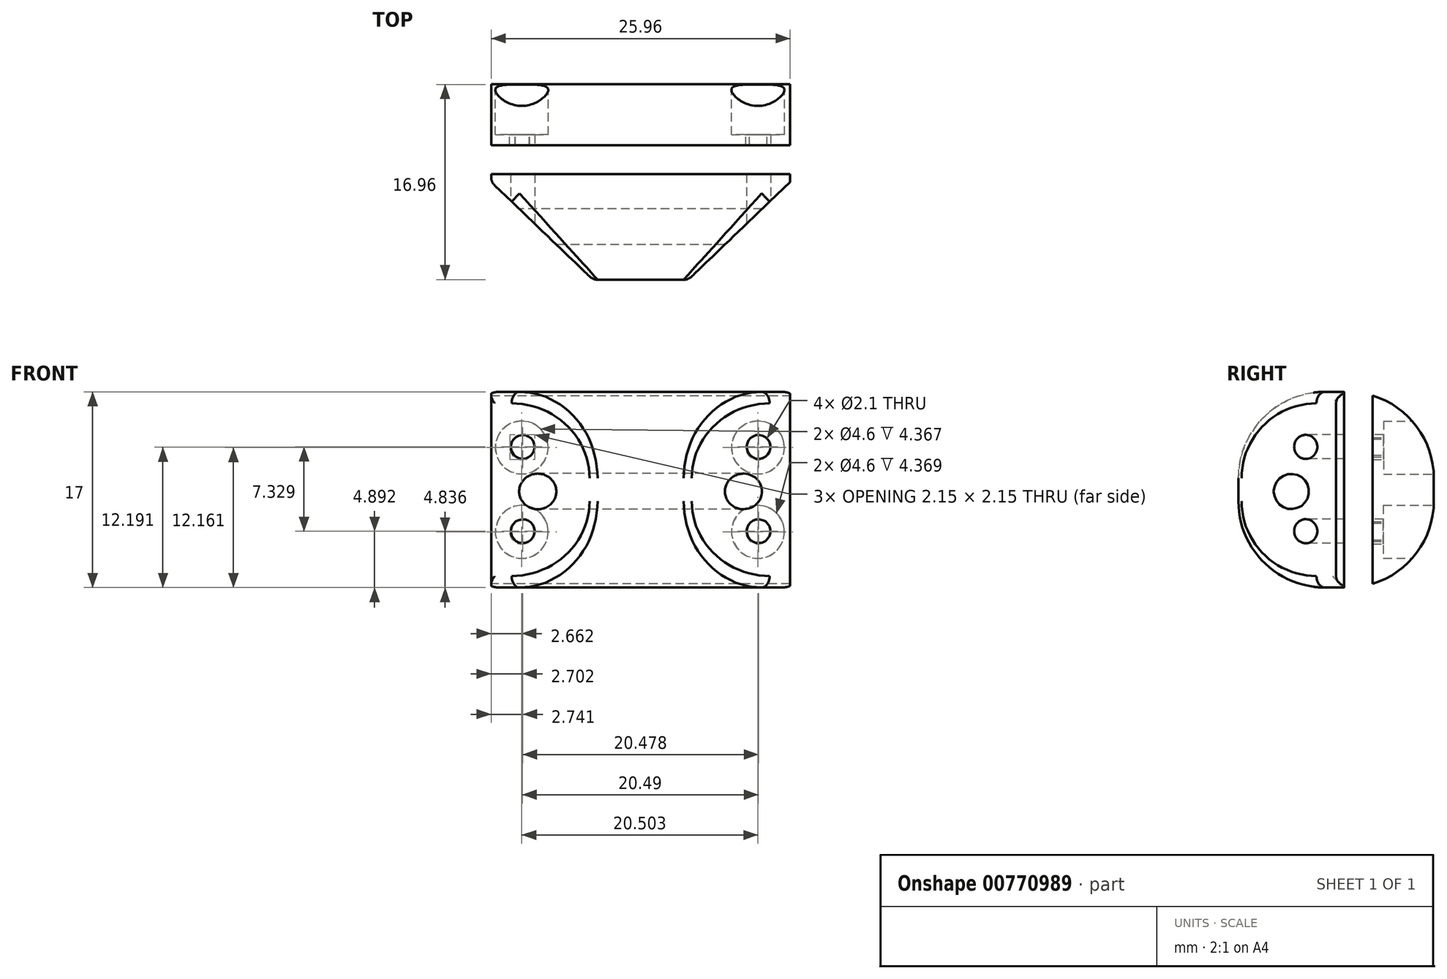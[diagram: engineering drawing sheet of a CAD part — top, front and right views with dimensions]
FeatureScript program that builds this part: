
annotation { "Feature Type Name" : "Feature", "Feature Type Description" : "" }
export const myFeature = defineFeature(function(context is Context, id is Id, definition is map)
    precondition{}
    {
        {
            var Q0;
            Q0=qCreatedBy(makeId("Top.planeOp"),FACE);
            var sketch = newSketch(context, id + "F0", { "sketchPlane" : qUnion([Q0])});
            skLineSegment(sketch, "E0.bottom", {"start": v(4.14, -8.48) * mm, "end": v(-4.14, -8.48) * mm});
            skLineSegment(sketch, "E0.top", {"start": v(12.98, 8.48) * mm, "end": v(-12.98, 8.48) * mm});
            skLineSegment(sketch, "E0.left", {"start": v(12.98, 0) * mm, "end": v(12.98, 8.48) * mm});
            skLineSegment(sketch, "E0.right", {"start": v(-12.98, 0) * mm, "end": v(-12.98, 8.48) * mm});
            skPoint(sketch, "E0.middle", {"position": v(0, 0) * mm});
            skLineSegment(sketch, "E1.top", {"start": v(-12.98, 8.48) * mm, "end": v(-4.14, 8.48) * mm});
            skLineSegment(sketch, "E2.top", {"start": v(12.98, 8.48) * mm, "end": v(4.14, 8.48) * mm});
            skLineSegment(sketch, "E3", {"start": v(-12.98, 0) * mm, "end": v(-4.14, -8.48) * mm});
            skLineSegment(sketch, "E4", {"start": v(4.14, -8.48) * mm, "end": v(12.98, 0) * mm});
            skPoint(sketch, "E5.orphan", {"position": v(12.98, -8.48) * mm});
            skPoint(sketch, "E6.orphan", {"position": v(-12.98, -8.48) * mm});
            skSolve(sketch);
        }
        {
            var Q0;
            Q0=makeQuery(id+"F0.imprint","IMPRINT",FACE,{"disambiguationData":[TD([[makeQuery(id+"F0.imprint","IMPRINT",EDGE,{"derivedFrom":sQuery(id+"F0.wireOp",EDGE,"E0.bottom")}),-1.0]])]});
            extrude(context, id + "F1", {"entities" : qUnion([Q0]), "depth" : 17 * mm, "offsetDistance" : 25 * mm});
        }
        {
            var Q0;
            Q0=makeQuery(id+"F1.opExtrude","CAP_EDGE",EDGE,{"disambiguationData":[OSD([sQuery(id+"F0.wireOp",EDGE,"E0.bottom")])],"isStart":false});
            var Q1;
            Q1=makeQuery(id+"F1.opExtrude","CAP_EDGE",EDGE,{"disambiguationData":[OSD([sQuery(id+"F0.wireOp",EDGE,"E0.bottom")])],"isStart":true});
            var Q2;
            Q2=makeQuery(id+"F1.opExtrude","CAP_EDGE",EDGE,{"disambiguationData":[OSD([sQuery(id+"F0.wireOp",EDGE,"E0.top"),sQuery(id+"F0.wireOp",EDGE,"E1.top"),sQuery(id+"F0.wireOp",EDGE,"E2.top")])],"isStart":false});
            var Q3;
            Q3=makeQuery(id+"F1.opExtrude","CAP_EDGE",EDGE,{"disambiguationData":[OSD([sQuery(id+"F0.wireOp",EDGE,"E0.top"),sQuery(id+"F0.wireOp",EDGE,"E1.top"),sQuery(id+"F0.wireOp",EDGE,"E2.top")])],"isStart":true});
            fillet(context, id + "F2", {"entities" : qUnion([Q0, Q1, Q2, Q3]), "radius" : 7.5 * mm, "tangentPropagation" : true, "allowEdgeOverflow" : false});
        }
        {
            var Q0;
            Q0=makeQuery(id+"F1.opExtrude","SWEPT_FACE",FACE,{"disambiguationData":[OSD([sQuery(id+"F0.wireOp",EDGE,"E0.right")])]});
            var sketch = newSketch(context, id + "F3", { "sketchPlane" : qUnion([Q0])});
            skLineSegment(sketch, "E7", {"start": v(3.88, 8.35) * mm, "end": v(-9.13, 9.1) * mm});
            skCircle(sketch, "E8", {"center": v(3.88, 8.35) * mm, "radius": 1.55 * mm});
            skSolve(sketch);
        }
        {
            var Q0;
            Q0=sQuery(id+"F3.wireOp",VERTEX,"E7.start");
            var Q1;
            Q1=makeQuery(id+"F1.opExtrude","SWEPT_BODY",BODY,{"disambiguationData":[OSD([sQuery(id+"F0.wireOp",EDGE,"E0.bottom"),sQuery(id+"F0.wireOp",EDGE,"E0.top"),sQuery(id+"F0.wireOp",EDGE,"E0.left"),sQuery(id+"F0.wireOp",EDGE,"E0.right"),sQuery(id+"F0.wireOp",EDGE,"E1.top"),sQuery(id+"F0.wireOp",EDGE,"E2.top"),sQuery(id+"F0.wireOp",EDGE,"E3"),sQuery(id+"F0.wireOp",EDGE,"E4")])]});
            hole(context, id + "F4", {"style" : HoleStyle.SIMPLE, "endStyle" : HoleEndStyle.THROUGH, "holeDiameter" : 3.1 * mm, "majorDiameter" : 5 * mm, "isTappedThrough" : true, "tappedDepth" : 12 * mm, "tapClearance" : 3, "locations" : qUnion([Q0]), "scope" : qUnion([Q1])});
        }
        {
            var Q0;
            Q0=makeQuery(id+"F1.opExtrude","SWEPT_EDGE",EDGE,{"disambiguationData":[OSD([sQuery(id+"F0.wireOp",EDGE,"E0.right"),sQuery(id+"F0.wireOp",EDGE,"E3")])]});
            var Q1;
            Q1=makeQuery(id+"F2.opFillet","BLEND_EDGE",EDGE,{"blendedFrom":[makeQuery(id+"F1.opExtrude","CAP_EDGE",EDGE,{"disambiguationData":[OSD([sQuery(id+"F0.wireOp",EDGE,"E0.bottom")])],"isStart":true}),makeQuery(id+"F1.opExtrude","SWEPT_FACE",FACE,{"disambiguationData":[OSD([sQuery(id+"F0.wireOp",EDGE,"E3")])]})],"blendedInto":[makeQuery(id+"F1.opExtrude","SWEPT_FACE",FACE,{"disambiguationData":[OSD([sQuery(id+"F0.wireOp",EDGE,"E3")])]})]});
            fillet(context, id + "F5", {"entities" : qUnion([Q0, Q1]), "radius" : 1 * mm, "allowEdgeOverflow" : false});
        }
        {
            var Q0;
            Q0=makeQuery(id+"F1.opExtrude","SWEPT_EDGE",EDGE,{"disambiguationData":[OSD([sQuery(id+"F0.wireOp",EDGE,"E0.bottom"),sQuery(id+"F0.wireOp",EDGE,"E4")])]});
            var Q1;
            Q1=makeQuery(id+"F2.opFillet","BLEND_EDGE",EDGE,{"blendedFrom":[makeQuery(id+"F1.opExtrude","CAP_EDGE",EDGE,{"disambiguationData":[OSD([sQuery(id+"F0.wireOp",EDGE,"E0.bottom")])],"isStart":true}),makeQuery(id+"F1.opExtrude","SWEPT_FACE",FACE,{"disambiguationData":[OSD([sQuery(id+"F0.wireOp",EDGE,"E4")])]})],"blendedInto":[makeQuery(id+"F1.opExtrude","SWEPT_FACE",FACE,{"disambiguationData":[OSD([sQuery(id+"F0.wireOp",EDGE,"E4")])]})]});
            fillet(context, id + "F6", {"entities" : qUnion([Q0, Q1]), "radius" : 1 * mm, "tangentPropagation" : true, "allowEdgeOverflow" : false});
        }
        {
            var Q0;
            Q0=qCreatedBy(makeId("Top.planeOp"),FACE);
            var sketch = newSketch(context, id + "F7", { "sketchPlane" : qUnion([Q0])});
            skLineSegment(sketch, "E9.bottom", {"start": v(-13, 0.68) * mm, "end": v(13, 0.68) * mm});
            skLineSegment(sketch, "E9.top", {"start": v(-13, 3.18) * mm, "end": v(13, 3.18) * mm});
            skLineSegment(sketch, "E9.left", {"start": v(-13, 0.68) * mm, "end": v(-13, 3.18) * mm});
            skLineSegment(sketch, "E9.right", {"start": v(13, 0.68) * mm, "end": v(13, 3.18) * mm});
            skSolve(sketch);
        }
        {
            var Q0;
            Q0=makeQuery(id+"F7.imprint","IMPRINT",FACE,{"disambiguationData":[TD([[makeQuery(id+"F7.imprint","IMPRINT",EDGE,{"derivedFrom":sQuery(id+"F7.wireOp",EDGE,"E9.bottom")}),1.0]])]});
            extrude(context, id + "F8", {"entities" : qUnion([Q0]), "operationType" : NewBodyOperationType.REMOVE, "oppositeDirection" : true, "depth" : -17.3 * mm, "offsetDistance" : 25 * mm});
        }
        {
            var Q0;
            Q0=makeQuery(id+"F1.opExtrude","SWEPT_FACE",FACE,{"disambiguationData":[OSD([sQuery(id+"F0.wireOp",EDGE,"E0.bottom")])]});
            var sketch = newSketch(context, id + "F9", { "sketchPlane" : qUnion([Q0])});
            skLineSegment(sketch, "E10.bottom", {"start": v(13, 0) * mm, "end": v(-13, 0) * mm});
            skLineSegment(sketch, "E10.top", {"start": v(13, 17.11) * mm, "end": v(-13, 17.11) * mm});
            skLineSegment(sketch, "E10.left", {"start": v(13, 0) * mm, "end": v(13, 17.11) * mm});
            skLineSegment(sketch, "E10.right", {"start": v(-13, 0) * mm, "end": v(-13, 17.11) * mm});
            skPoint(sketch, "E10.middle", {"position": v(0, 8.56) * mm});
            skPoint(sketch, "E11.top.end.orphan", {"position": v(10.24, 2.7) * mm});
            skPoint(sketch, "E11.bottom.end.orphan", {"position": v(10.24, 14.41) * mm});
            skPoint(sketch, "E11.left.end.orphan", {"position": v(-10.24, 2.7) * mm});
            skPoint(sketch, "E11.left.start.orphan", {"position": v(-10.24, 14.41) * mm});
            skLineSegment(sketch, "E12.bottom", {"start": v(-10.24, 12.22) * mm, "end": v(10.24, 12.22) * mm});
            skLineSegment(sketch, "E12.top", {"start": v(-10.24, 4.9) * mm, "end": v(10.24, 4.9) * mm});
            skLineSegment(sketch, "E12.left", {"start": v(-10.24, 12.22) * mm, "end": v(-10.24, 4.9) * mm});
            skLineSegment(sketch, "E12.right", {"start": v(10.24, 12.22) * mm, "end": v(10.24, 4.9) * mm});
            skLineSegment(sketch, "E13.bottom", {"start": v(10.24, 12.22) * mm, "end": v(-10.24, 12.22) * mm});
            skLineSegment(sketch, "E13.top", {"start": v(10.24, 4.9) * mm, "end": v(-10.24, 4.9) * mm});
            skSolve(sketch);
        }
        {
            var Q0;
            Q0=sQuery(id+"F9.wireOp",VERTEX,"E12.bottom.start");
            var Q1;
            Q1=sQuery(id+"F9.wireOp",VERTEX,"E12.top.start");
            var Q2;
            Q2=sQuery(id+"F9.wireOp",VERTEX,"E12.top.end");
            var Q3;
            Q3=sQuery(id+"F9.wireOp",VERTEX,"E12.bottom.end");
            var Q4;
            Q4=makeQuery(id+"F8.boolean.opBoolean","SPLIT",BODY,{"disambiguationData":[OD(0.0)],"derivedFrom":makeQuery(id+"F1.opExtrude","SWEPT_BODY",BODY,{"disambiguationData":[OSD([sQuery(id+"F0.wireOp",EDGE,"E0.bottom"),sQuery(id+"F0.wireOp",EDGE,"E0.top"),sQuery(id+"F0.wireOp",EDGE,"E0.left"),sQuery(id+"F0.wireOp",EDGE,"E0.right"),sQuery(id+"F0.wireOp",EDGE,"E1.top"),sQuery(id+"F0.wireOp",EDGE,"E2.top"),sQuery(id+"F0.wireOp",EDGE,"E3"),sQuery(id+"F0.wireOp",EDGE,"E4")])]})});
            var Q5;
            Q5=makeQuery(id+"F8.boolean.opBoolean","SPLIT",BODY,{"disambiguationData":[OD(1.0)],"derivedFrom":makeQuery(id+"F1.opExtrude","SWEPT_BODY",BODY,{"disambiguationData":[OSD([sQuery(id+"F0.wireOp",EDGE,"E0.bottom"),sQuery(id+"F0.wireOp",EDGE,"E0.top"),sQuery(id+"F0.wireOp",EDGE,"E0.left"),sQuery(id+"F0.wireOp",EDGE,"E0.right"),sQuery(id+"F0.wireOp",EDGE,"E1.top"),sQuery(id+"F0.wireOp",EDGE,"E2.top"),sQuery(id+"F0.wireOp",EDGE,"E3"),sQuery(id+"F0.wireOp",EDGE,"E4")])]})});
            hole(context, id + "F10", {"style" : HoleStyle.SIMPLE, "endStyle" : HoleEndStyle.BLIND, "holeDiameter" : 2.1 * mm, "majorDiameter" : 5 * mm, "holeDepth" : 12 * mm, "isTappedThrough" : true, "tappedDepth" : 12 * mm, "tapClearance" : 3, "locations" : qUnion([Q0, Q1, Q2, Q3]), "scope" : qUnion([Q4, Q5])});
        }
        {
            var Q0;
            Q0=makeQuery(id+"F1.opExtrude","SWEPT_FACE",FACE,{"disambiguationData":[OSD([sQuery(id+"F0.wireOp",EDGE,"E0.top"),sQuery(id+"F0.wireOp",EDGE,"E1.top"),sQuery(id+"F0.wireOp",EDGE,"E2.top")])]});
            var sketch = newSketch(context, id + "F11", { "sketchPlane" : qUnion([Q0])});
            skLineSegment(sketch, "E14.bottom", {"start": v(-10.19, 12.16) * mm, "end": v(10.32, 12.16) * mm});
            skLineSegment(sketch, "E14.top", {"start": v(-10.19, 4.84) * mm, "end": v(10.32, 4.84) * mm});
            skLineSegment(sketch, "E14.left", {"start": v(-10.19, 12.16) * mm, "end": v(-10.19, 4.84) * mm});
            skLineSegment(sketch, "E14.right", {"start": v(10.32, 12.16) * mm, "end": v(10.32, 4.84) * mm});
            skSolve(sketch);
        }
        {
            var Q0;
            Q0=sQuery(id+"F11.wireOp",VERTEX,"E14.top.start");
            var Q1;
            Q1=sQuery(id+"F11.wireOp",VERTEX,"E14.bottom.start");
            var Q2;
            Q2=sQuery(id+"F11.wireOp",VERTEX,"E14.bottom.end");
            var Q3;
            Q3=sQuery(id+"F11.wireOp",VERTEX,"E14.top.end");
            var Q4;
            Q4=makeQuery(id+"F8.boolean.opBoolean","SPLIT",BODY,{"disambiguationData":[OD(0.0)],"derivedFrom":makeQuery(id+"F1.opExtrude","SWEPT_BODY",BODY,{"disambiguationData":[OSD([sQuery(id+"F0.wireOp",EDGE,"E0.bottom"),sQuery(id+"F0.wireOp",EDGE,"E0.top"),sQuery(id+"F0.wireOp",EDGE,"E0.left"),sQuery(id+"F0.wireOp",EDGE,"E0.right"),sQuery(id+"F0.wireOp",EDGE,"E1.top"),sQuery(id+"F0.wireOp",EDGE,"E2.top"),sQuery(id+"F0.wireOp",EDGE,"E3"),sQuery(id+"F0.wireOp",EDGE,"E4")])]})});
            hole(context, id + "F12", {"style" : HoleStyle.C_BORE, "endStyle" : HoleEndStyle.BLIND, "holeDiameter" : 2.1 * mm, "cBoreDiameter" : 4.6 * mm, "cBoreDepth" : 2.5 * mm, "majorDiameter" : 5 * mm, "holeDepth" : 4 * mm, "isTappedThrough" : true, "tappedDepth" : 12 * mm, "tapClearance" : 3, "locations" : qUnion([Q0, Q1, Q2, Q3]), "scope" : qUnion([Q4])});
        }
    });
